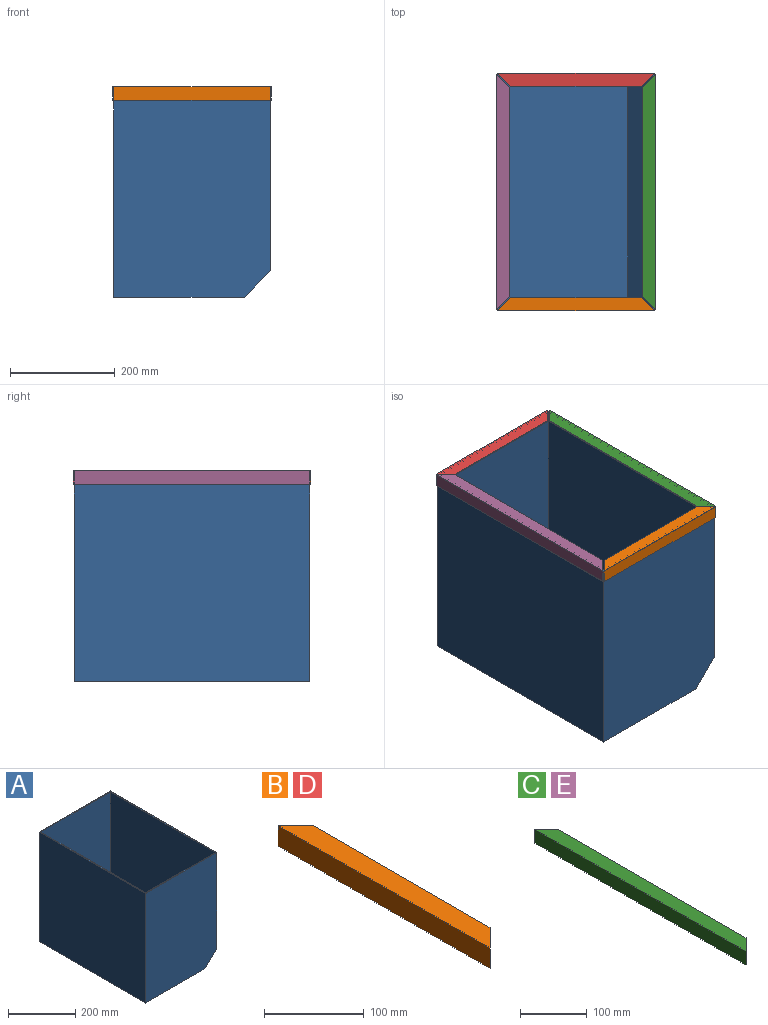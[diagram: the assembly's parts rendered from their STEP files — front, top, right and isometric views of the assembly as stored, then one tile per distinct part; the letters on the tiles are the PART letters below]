
ASSEMBLY  parts=5 mates=4
PART A: 13 faces, bbox 300x450x400 mm
  f0: plane 450x300mm, normal (0,0,1), area 5201mm2, adj f1,f2,f4,f5,f7,f8,f10,f11
  f1: plane 450x350mm, normal (1,0,0), area 157500mm2, adj f0,f4,f5,f6
  f2: plane 450x400mm, normal (-1,0,0), area 180000mm2, adj f0,f3,f4,f5
  f3: plane 450x250mm, normal (0,0,-1), area 112500mm2, adj f2,f4,f5,f6
  f4: plane 400x300mm, normal (0,-1,0), area 118750mm2, adj f0,f1,f2,f3,f6
  f5: plane 400x300mm, normal (0,1,0), area 118750mm2, adj f0,f1,f2,f3,f6
  f6: plane 450x50mm, normal (0.71,0,-0.71), area 31819.8mm2, adj f1,f3,f4,f5
  f7: plane 443x348.55mm, normal (-1,0,0), area 154407.8mm2, adj f0,f10,f11,f12
  f8: plane 443x396.5mm, normal (1,0,0), area 175649.5mm2, adj f0,f9,f10,f11
  f9: plane 443x245.05mm, normal (0,0,1), area 108557.3mm2, adj f8,f10,f11,f12
  f10: plane 396.5x293mm, normal (0,1,0), area 115024.9mm2, adj f0,f7,f8,f9,f12
  f11: plane 396.5x293mm, normal (0,-1,0), area 115024.9mm2, adj f0,f7,f8,f9,f12
  f12: plane 443x47.95mm, normal (-0.71,0,0.71), area 30040.4mm2, adj f7,f9,f10,f11
PART B: 8 faces, bbox 25x300x25 mm
  f0: plane 300x25mm, normal (0,0,1), area 6875mm2, adj f1,f5,f6,f7
  f1: plane 300x25mm, normal (-1,0,0), area 7500mm2, adj f0,f2,f6,f7
  f2: plane 300x2mm, normal (0,0,-1), area 596mm2, adj f1,f3,f6,f7
  f3: plane 296x23mm, normal (1,0,0), area 6808mm2, adj f2,f4,f6,f7
  f4: plane 296x23mm, normal (0,0,-1), area 6279mm2, adj f3,f5,f6,f7
  f5: plane 250x2mm, normal (1,0,0), area 500mm2, adj f0,f4,f6,f7
  f6: plane 25x25mm, normal (0.71,0.71,0), area 135.8mm2, adj f0,f1,f2,f3,f4,f5
  f7: plane 25x25mm, normal (0.71,-0.71,0), area 135.8mm2, adj f0,f1,f2,f3,f4,f5
PART C: 8 faces, bbox 25x450x25 mm
  f0: plane 450x25mm, normal (0,0,1), area 10625mm2, adj f1,f5,f6,f7
  f1: plane 450x25mm, normal (-1,0,0), area 11250mm2, adj f0,f2,f6,f7
  f2: plane 450x2mm, normal (0,0,-1), area 896mm2, adj f1,f3,f6,f7
  f3: plane 446x23mm, normal (1,0,0), area 10258mm2, adj f2,f4,f6,f7
  f4: plane 446x23mm, normal (0,0,-1), area 9729mm2, adj f3,f5,f6,f7
  f5: plane 400x2mm, normal (1,0,0), area 800mm2, adj f0,f4,f6,f7
  f6: plane 25x25mm, normal (0.71,-0.71,0), area 135.8mm2, adj f0,f1,f2,f3,f4,f5
  f7: plane 25x25mm, normal (0.71,0.71,0), area 135.8mm2, adj f0,f1,f2,f3,f4,f5
PART D: same geometry as B
PART E: same geometry as C
PLACE A at identity fixed
PLACE B rot(axis=(0,0,1),90deg) t=(0,-214.5,189.5)mm
PLACE C rot(axis=(0,0,1),180deg) t=(139.5,0,189.5)mm
PLACE D rot(axis=(0,0,-1),90deg) t=(0,214.5,189.5)mm
PLACE E t=(-139.5,0,189.5)mm
MATE fastened D.f3 <-> A.f5  axis (0,-1,0) through (0,225,200)mm
MATE fastened A.f2 <-> E.f3  axis (-1,0,0) through (-150,0,200)mm
MATE fastened B.f3 <-> A.f4  axis (0,1,0) through (0,-225,200)mm
MATE fastened C.f3 <-> A.f1  axis (-1,0,0) through (150,0,200)mm
